# Revit family: NewTechWood-UltraEasy_Fencing-Fence
name_source: partatom
category: Specialty Equipment
units: mm (PartAtom-declared; Revit-internal decimal feet)

## family parameters
Always vertical = Yes
Cut with Voids When Loaded = No
Enable Cutting in Views = No
Maintain Annotation Orientation = No
Part Type = Normal
Room Calculation Point = No
Round Connector Dimension = Use Diameter
Shared = No
Work Plane-Based = No

## types (3) — shared parameters
Construction Details = https://www.arcat.com
Description = UltraShield® Naturale™ UltraEasy Fence, 71" Width (Maximum) x 72" Height x 1.125" Thickness, With Capped Composite Board, 6" Height x 0.8" Thickness x 69" Width (Maximum)
Fence Height = 72 "
Installation-Fabrication = https://www.newtechwood.com
Manufacturer = NewTechWood America Inc.
Manufacturer Fax = 1-281-661-1167
Panel Thickness = 1 "
Post Height = 75 "
Product Data = https://www.arcat.com
Product Properties = https://www.newtechwood.com
Sales Information = https://www.newtechwood.com
URL = https://www.newtechwood.com
zero-valued in all types: Default Elevation

## per-type parameters (varying)
| type | Model | UH105 Fence Profile | UH24 Fence Profile | UH66 Fence Profile |
| UH66 | Fence UH66 | No | No | Yes |
| UH105 | Fence UH105 | Yes | No | No |
| UH24 | Fence UH24 | No | Yes | No |

## geometry (parser evidence)
native form markers: Sweep x4
no freeform markers — native parametric forms only
